# Revit family: BESTA BURS wall shelf
name_source: partatom
category: Furniture
revit_build: Autodesk Revit Architecture 2012 (Build: 20110309_2315(x64)
units: mm (PartAtom-declared; Revit-internal decimal feet)

## types (4) — shared parameters
Cost = 101.11 $
IKEA Handle = IKEA Aluminium
IKEA body = IKEA White
Manufacturer = IKEA
depth = 260 mm  [stored 0.853018 ft]
height = 260 mm  [stored 0.853018 ft]
width = 1800 mm  [stored 5.90551 ft]

## per-type parameters (varying)
| type | IKEA Door | Model |
| BESTA Burs wall  shelf 180x26 High Gloss White | IKEA High Gloss White | 701.037.59 |
| BESTA Burs wall  shelf 180x26 High Gloss Red | IKEA High Gloss Red | 701.037.59 |
| BESTA Burs wall  shelf 180x26 High Gloss Black | IKEA High Gloss Black | 601.339.31 |
| BESTA Burs wall  shelf 180x26 High Gloss Grey | IKEA High Gloss Grey | 301.783.94 |

note: [stored X ft] marks values corroborated as IEEE doubles in the binary element streams (Revit-internal decimal feet)

## geometry (parser evidence)
native form markers: Sweep x5
no freeform markers — native parametric forms only
